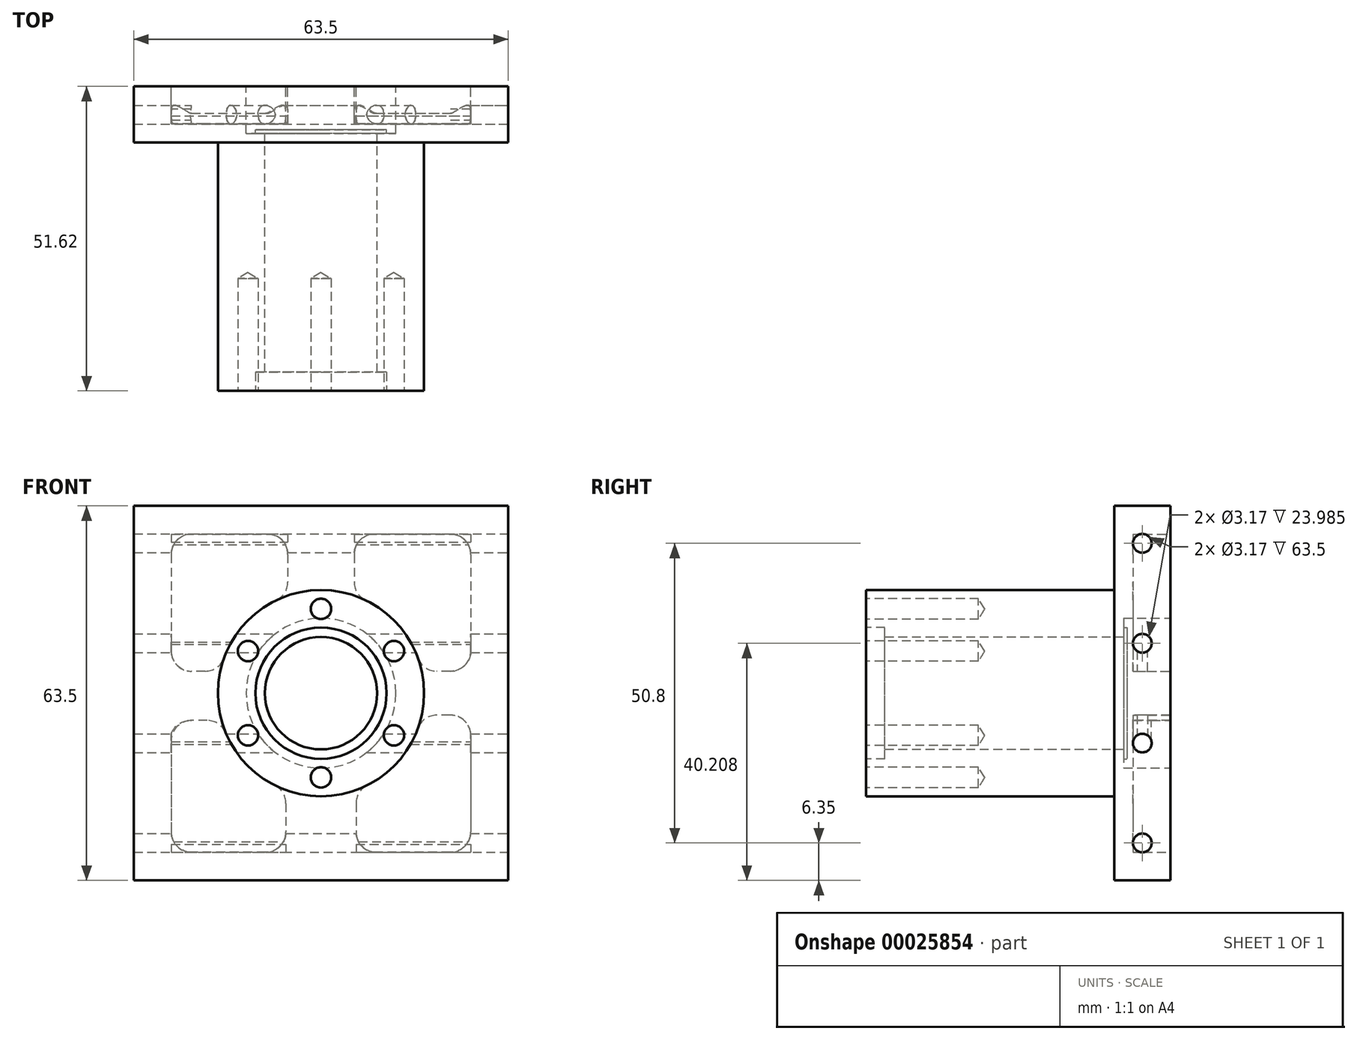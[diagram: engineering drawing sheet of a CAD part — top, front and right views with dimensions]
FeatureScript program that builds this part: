
annotation { "Feature Type Name" : "Feature", "Feature Type Description" : "" }
export const myFeature = defineFeature(function(context is Context, id is Id, definition is map)
    precondition{}
    {
        {
            var Q0;
            Q0=qCreatedBy(makeId("Front.planeOp"),FACE);
            var sketch = newSketch(context, id + "F0", { "sketchPlane" : qUnion([Q0])});
            skLineSegment(sketch, "E0.rect.bottom", {"start": v(-31.75, 31.75) * mm, "end": v(31.75, 31.75) * mm});
            skLineSegment(sketch, "E0.rect.top", {"start": v(-31.75, -31.75) * mm, "end": v(31.75, -31.75) * mm});
            skLineSegment(sketch, "E0.rect.left", {"start": v(-31.75, 31.75) * mm, "end": v(-31.75, -31.75) * mm});
            skLineSegment(sketch, "E0.rect.right", {"start": v(31.75, 31.75) * mm, "end": v(31.75, -31.75) * mm});
            skPoint(sketch, "E0.rect.middle", {"position": v(0, 0) * mm});
            skSolve(sketch);
        }
        {
            var Q0;
            Q0 = qSketchRegion(id + "F0", true);
            extrude(context, id + "F1", {"entities" : qUnion([Q0]), "oppositeDirection" : true, "depth" : 9.52 * mm});
        }
        {
            var Q0;
            Q0=makeQuery(id+"F1.opExtrude","SWEPT_FACE",FACE,{"disambiguationData":[OSD([sQuery(id+"F0.wireOp",EDGE,"E0.rect.right")])]});
            var sketch = newSketch(context, id + "F2", { "sketchPlane" : qUnion([Q0])});
            skLineSegment(sketch, "E1", {"start": v(4.75, 33.77) * mm, "end": v(4.75, -39.78) * mm});
            skPoint(sketch, "E2", {"position": v(4.75, 25.4) * mm});
            skPoint(sketch, "E3", {"position": v(4.75, 8.46) * mm});
            skPoint(sketch, "E4", {"position": v(4.75, -8.46) * mm});
            skPoint(sketch, "E5", {"position": v(4.75, -25.4) * mm});
            skSolve(sketch);
        }
        {
            var Q0;
            Q0=sQuery(id+"F2.wireOp",VERTEX,"E2");
            var Q1;
            Q1=sQuery(id+"F2.wireOp",VERTEX,"E3");
            var Q2;
            Q2=sQuery(id+"F2.wireOp",VERTEX,"E4");
            var Q3;
            Q3=sQuery(id+"F2.wireOp",VERTEX,"E5");
            var Q4;
            Q4=makeQuery(id+"F1.opExtrude","SWEPT_BODY",BODY,{"disambiguationData":[OSD([sQuery(id+"F0.wireOp",EDGE,"E0.rect.bottom"),sQuery(id+"F0.wireOp",EDGE,"E0.rect.top"),sQuery(id+"F0.wireOp",EDGE,"E0.rect.left"),sQuery(id+"F0.wireOp",EDGE,"E0.rect.right")])]});
            hole(context, id + "F3", {"style" : HoleStyle.SIMPLE, "holeDiameter" : 3.17 * mm, "endStyle" : HoleEndStyle.THROUGH, "locations" : qUnion([Q0, Q1, Q2, Q3]), "scope" : qUnion([Q4])});
        }
        {
            var Q0;
            Q0=makeQuery(id+"F1.opExtrude","CAP_FACE",FACE,{"disambiguationData":[OSD([sQuery(id+"F0.wireOp",EDGE,"E0.rect.bottom"),sQuery(id+"F0.wireOp",EDGE,"E0.rect.top"),sQuery(id+"F0.wireOp",EDGE,"E0.rect.left"),sQuery(id+"F0.wireOp",EDGE,"E0.rect.right")])],"isStart":true});
            var sketch = newSketch(context, id + "F4", { "sketchPlane" : qUnion([Q0])});
            skCircle(sketch, "E6", {"center": v(0, 0) * mm, "radius": 17.49 * mm});
            skSolve(sketch);
        }
        {
            var Q0;
            Q0 = qSketchRegion(id + "F4", true);
            extrude(context, id + "F5", {"entities" : qUnion([Q0]), "operationType" : NewBodyOperationType.ADD, "depth" : 42.1 * mm});
        }
        {
            var Q0;
            Q0=makeQuery(id+"F5.opExtrude","CAP_FACE",FACE,{"disambiguationData":[OSD([sQuery(id+"F4.wireOp",EDGE,"E6")])],"isStart":false});
            var sketch = newSketch(context, id + "F6", { "sketchPlane" : qUnion([Q0])});
            skCircle(sketch, "E7", {"center": v(0, 0) * mm, "radius": 14.29 * mm});
            skCircle(sketch, "E8.cCircle", {"center": v(0, 0) * mm, "radius": 14.29 * mm, "construction": true});
            skLineSegment(sketch, "E8.0", {"start": v(0, 14.29) * mm, "end": v(12.37, 7.14) * mm});
            skLineSegment(sketch, "E8.1", {"start": v(12.37, 7.14) * mm, "end": v(12.37, -7.14) * mm});
            skLineSegment(sketch, "E8.2", {"start": v(12.37, -7.14) * mm, "end": v(0, -14.29) * mm});
            skLineSegment(sketch, "E8.3", {"start": v(0, -14.29) * mm, "end": v(-12.37, -7.14) * mm});
            skLineSegment(sketch, "E8.4", {"start": v(-12.37, -7.14) * mm, "end": v(-12.37, 7.14) * mm});
            skLineSegment(sketch, "E8.5", {"start": v(-12.37, 7.14) * mm, "end": v(0, 14.29) * mm});
            skSolve(sketch);
        }
        {
            var Q0;
            Q0=sQuery(id+"F6.wireOp",VERTEX,"E8.0.start");
            var Q1;
            Q1=sQuery(id+"F6.wireOp",VERTEX,"E8.4.end");
            var Q2;
            Q2=sQuery(id+"F6.wireOp",VERTEX,"E8.3.end");
            var Q3;
            Q3=sQuery(id+"F6.wireOp",VERTEX,"E8.3.start");
            var Q4;
            Q4=sQuery(id+"F6.wireOp",VERTEX,"E8.2.start");
            var Q5;
            Q5=sQuery(id+"F6.wireOp",VERTEX,"E8.1.start");
            var Q6;
            Q6=makeQuery(id+"F1.opExtrude","SWEPT_BODY",BODY,{"disambiguationData":[OSD([sQuery(id+"F0.wireOp",EDGE,"E0.rect.bottom"),sQuery(id+"F0.wireOp",EDGE,"E0.rect.top"),sQuery(id+"F0.wireOp",EDGE,"E0.rect.left"),sQuery(id+"F0.wireOp",EDGE,"E0.rect.right")])]});
            hole(context, id + "F7", {"style" : HoleStyle.SIMPLE, "holeDiameter" : 3.45 * mm, "endStyle" : HoleEndStyle.BLIND, "holeDepth" : 19.05 * mm, "locations" : qUnion([Q0, Q1, Q2, Q3, Q4, Q5]), "scope" : qUnion([Q6])});
        }
        {
            var Q0;
            Q0=makeQuery(id+"F1.opExtrude","CAP_FACE",FACE,{"disambiguationData":[OSD([sQuery(id+"F0.wireOp",EDGE,"E0.rect.bottom"),sQuery(id+"F0.wireOp",EDGE,"E0.rect.top"),sQuery(id+"F0.wireOp",EDGE,"E0.rect.left"),sQuery(id+"F0.wireOp",EDGE,"E0.rect.right")])],"isStart":false});
            var sketch = newSketch(context, id + "F8", { "sketchPlane" : qUnion([Q0])});
            skCircle(sketch, "E9", {"center": v(0, 0) * mm, "radius": 9.53 * mm});
            skSolve(sketch);
        }
        {
            var Q0;
            Q0 = qSketchRegion(id + "F8", true);
            extrude(context, id + "F9", {"entities" : qUnion([Q0]), "operationType" : NewBodyOperationType.REMOVE, "oppositeDirection" : true, "depth" : 71.13 * mm});
        }
        {
            var Q0;
            Q0=makeQuery(id+"F1.opExtrude","CAP_FACE",FACE,{"disambiguationData":[OSD([sQuery(id+"F0.wireOp",EDGE,"E0.rect.bottom"),sQuery(id+"F0.wireOp",EDGE,"E0.rect.top"),sQuery(id+"F0.wireOp",EDGE,"E0.rect.left"),sQuery(id+"F0.wireOp",EDGE,"E0.rect.right")])],"isStart":false});
            var sketch = newSketch(context, id + "F10", { "sketchPlane" : qUnion([Q0])});
            skCircle(sketch, "E10", {"center": v(0, 0) * mm, "radius": 11.13 * mm});
            skSolve(sketch);
        }
        {
            var Q0;
            Q0 = qSketchRegion(id + "F10", true);
            extrude(context, id + "F11", {"entities" : qUnion([Q0]), "operationType" : NewBodyOperationType.REMOVE, "oppositeDirection" : true, "depth" : 7.37 * mm});
        }
        {
            var Q0;
            Q0=makeQuery(id+"F1.opExtrude","CAP_FACE",FACE,{"disambiguationData":[OSD([sQuery(id+"F0.wireOp",EDGE,"E0.rect.bottom"),sQuery(id+"F0.wireOp",EDGE,"E0.rect.top"),sQuery(id+"F0.wireOp",EDGE,"E0.rect.left"),sQuery(id+"F0.wireOp",EDGE,"E0.rect.right")])],"isStart":false});
            var sketch = newSketch(context, id + "F12", { "sketchPlane" : qUnion([Q0])});
            skCircle(sketch, "E11", {"center": v(0, 0) * mm, "radius": 12.7 * mm});
            skSolve(sketch);
        }
        {
            var Q0;
            Q0=makeQuery(id+"F12.imprint","IMPRINT",FACE,{"disambiguationData":[TD([[makeQuery(id+"F12.imprint","IMPRINT",EDGE,{"derivedFrom":sQuery(id+"F12.wireOp",EDGE,"E11")}),1.0]])]});
            extrude(context, id + "F13", {"entities" : qUnion([Q0]), "operationType" : NewBodyOperationType.REMOVE, "oppositeDirection" : true, "depth" : 7.95 * mm});
        }
        {
            var Q0;
            Q0=makeQuery(id+"F5.opExtrude","CAP_FACE",FACE,{"disambiguationData":[OSD([sQuery(id+"F4.wireOp",EDGE,"E6")])],"isStart":false});
            var sketch = newSketch(context, id + "F14", { "sketchPlane" : qUnion([Q0])});
            skCircle(sketch, "E12", {"center": v(0, 0) * mm, "radius": 11.13 * mm});
            skSolve(sketch);
        }
        {
            var Q0;
            Q0 = qSketchRegion(id + "F14", true);
            extrude(context, id + "F15", {"entities" : qUnion([Q0]), "operationType" : NewBodyOperationType.REMOVE, "oppositeDirection" : true, "depth" : 3.17 * mm});
        }
        {
            var Q0;
            Q0=makeQuery(id+"F1.opExtrude","CAP_FACE",FACE,{"disambiguationData":[OSD([sQuery(id+"F0.wireOp",EDGE,"E0.rect.bottom"),sQuery(id+"F0.wireOp",EDGE,"E0.rect.top"),sQuery(id+"F0.wireOp",EDGE,"E0.rect.left"),sQuery(id+"F0.wireOp",EDGE,"E0.rect.right")])],"isStart":false});
            var sketch = newSketch(context, id + "F16", { "sketchPlane" : qUnion([Q0])});
            skLineSegment(sketch, "E13.rect.bottom", {"start": v(-25.4, 26.97) * mm, "end": v(-5.63, 26.97) * mm});
            skLineSegment(sketch, "E13.rect.top", {"start": v(-25.4, -26.97) * mm, "end": v(-5.95, -26.97) * mm});
            skLineSegment(sketch, "E13.rect.left", {"start": v(-25.4, 26.97) * mm, "end": v(-25.4, 3.73) * mm});
            skLineSegment(sketch, "E13.rect.right", {"start": v(25.4, 26.97) * mm, "end": v(25.4, 3.73) * mm});
            skPoint(sketch, "E13.rect.middle", {"position": v(0, 0) * mm});
            skArc(sketch, "E14", {"start": v(-5.63, 16.54) * mm, "mid": v(-13.04, 11.64) * mm, "end": v(-17.07, 3.73) * mm});
            skLineSegment(sketch, "E15", {"start": v(-5.63, 26.97) * mm, "end": v(-5.63, 16.54) * mm});
            skLineSegment(sketch, "E16", {"start": v(5.63, 26.97) * mm, "end": v(5.63, 16.54) * mm});
            skLineSegment(sketch, "E17", {"start": v(5.95, -16.43) * mm, "end": v(5.95, -26.97) * mm});
            skLineSegment(sketch, "E18", {"start": v(-5.95, -16.43) * mm, "end": v(-5.95, -26.97) * mm});
            skLineSegment(sketch, "E19", {"start": v(-25.4, -3.73) * mm, "end": v(-17.07, -3.73) * mm});
            skLineSegment(sketch, "E20", {"start": v(-25.4, 3.73) * mm, "end": v(-17.07, 3.73) * mm});
            skLineSegment(sketch, "E21", {"start": v(17.07, 3.73) * mm, "end": v(25.4, 3.73) * mm});
            skLineSegment(sketch, "E22", {"start": v(16.85, -4.63) * mm, "end": v(25.4, -4.63) * mm});
            skLineSegment(sketch, "E23.trimOffspring", {"start": v(5.63, 26.97) * mm, "end": v(25.4, 26.97) * mm});
            skArc(sketch, "E24.trimOffspring", {"start": v(-17.07, -3.73) * mm, "mid": v(-13.15, -11.51) * mm, "end": v(-5.95, -16.43) * mm});
            skLineSegment(sketch, "E25.trimOffspring", {"start": v(-25.4, -3.73) * mm, "end": v(-25.4, -26.97) * mm});
            skArc(sketch, "E26.trimOffspring", {"start": v(5.95, -16.43) * mm, "mid": v(12.84, -11.86) * mm, "end": v(16.85, -4.63) * mm});
            skLineSegment(sketch, "E27.trimOffspring", {"start": v(5.95, -26.97) * mm, "end": v(25.4, -26.97) * mm});
            skLineSegment(sketch, "E28.trimOffspring", {"start": v(25.4, -4.63) * mm, "end": v(25.4, -26.97) * mm});
            skArc(sketch, "E29.trimOffspring", {"start": v(17.07, 3.73) * mm, "mid": v(13.04, 11.64) * mm, "end": v(5.63, 16.54) * mm});
            skSolve(sketch);
        }
        {
            var Q0;
            Q0=makeQuery(id+"F16.imprint","IMPRINT",FACE,{"disambiguationData":[TD([[makeQuery(id+"F16.imprint","IMPRINT",EDGE,{"derivedFrom":sQuery(id+"F16.wireOp",EDGE,"E13.rect.bottom")}),-1.0]])]});
            var Q1;
            Q1=makeQuery(id+"F16.imprint","IMPRINT",FACE,{"disambiguationData":[TD([[makeQuery(id+"F16.imprint","IMPRINT",EDGE,{"derivedFrom":sQuery(id+"F16.wireOp",EDGE,"E13.rect.right")}),-1.0]])]});
            var Q2;
            Q2=makeQuery(id+"F16.imprint","IMPRINT",FACE,{"disambiguationData":[TD([[makeQuery(id+"F16.imprint","IMPRINT",EDGE,{"derivedFrom":sQuery(id+"F16.wireOp",EDGE,"E17")}),1.0]])]});
            var Q3;
            Q3=makeQuery(id+"F16.imprint","IMPRINT",FACE,{"disambiguationData":[TD([[makeQuery(id+"F16.imprint","IMPRINT",EDGE,{"derivedFrom":sQuery(id+"F16.wireOp",EDGE,"E13.rect.top")}),1.0]])]});
            extrude(context, id + "F17", {"entities" : qUnion([Q0, Q1, Q2, Q3]), "operationType" : NewBodyOperationType.REMOVE, "oppositeDirection" : true, "depth" : 6.35 * mm});
        }
        {
            var Q0;
            {var subQ0=sQuery(id+"F16.wireOp",EDGE,"E13.rect.bottom");var subQ1=sQuery(id+"F16.wireOp",EDGE,"E13.rect.left");Q0=makeQuery(id+"F17.boolean.opBoolean","COPY",EDGE,{"disambiguationData":[TD([makeQuery(id+"F1.opExtrude","CAP_FACE",FACE,{"disambiguationData":[OSD([sQuery(id+"F0.wireOp",EDGE,"E0.rect.bottom"),sQuery(id+"F0.wireOp",EDGE,"E0.rect.top"),sQuery(id+"F0.wireOp",EDGE,"E0.rect.left"),sQuery(id+"F0.wireOp",EDGE,"E0.rect.right")])],"isStart":false})])],"derivedFrom":makeQuery(id+"F17.opExtrude","SWEPT_EDGE",EDGE,{"disambiguationData":[OSD([subQ0,subQ1])]})});}
            var Q1;
            {var subQ0=sQuery(id+"F16.wireOp",EDGE,"E16");var subQ1=sQuery(id+"F16.wireOp",EDGE,"E23.trimOffspring");Q1=makeQuery(id+"F17.boolean.opBoolean","COPY",EDGE,{"disambiguationData":[TD([makeQuery(id+"F1.opExtrude","CAP_FACE",FACE,{"disambiguationData":[OSD([sQuery(id+"F0.wireOp",EDGE,"E0.rect.bottom"),sQuery(id+"F0.wireOp",EDGE,"E0.rect.top"),sQuery(id+"F0.wireOp",EDGE,"E0.rect.left"),sQuery(id+"F0.wireOp",EDGE,"E0.rect.right")])],"isStart":false})])],"derivedFrom":makeQuery(id+"F17.opExtrude","SWEPT_EDGE",EDGE,{"disambiguationData":[OSD([subQ0,subQ1])]})});}
            var Q2;
            Q2=makeQuery(id+"F17.boolean.opBoolean","COPY",EDGE,{"derivedFrom":makeQuery(id+"F17.opExtrude","SWEPT_EDGE",EDGE,{"disambiguationData":[OSD([sQuery(id+"F16.wireOp",EDGE,"E17"),sQuery(id+"F16.wireOp",EDGE,"E26.trimOffspring")])]})});
            var Q3;
            Q3=makeQuery(id+"F17.boolean.opBoolean","COPY",EDGE,{"derivedFrom":makeQuery(id+"F17.opExtrude","SWEPT_EDGE",EDGE,{"disambiguationData":[OSD([sQuery(id+"F16.wireOp",EDGE,"E22"),sQuery(id+"F16.wireOp",EDGE,"E26.trimOffspring")])]})});
            var Q4;
            Q4=makeQuery(id+"F17.boolean.opBoolean","COPY",EDGE,{"derivedFrom":makeQuery(id+"F17.opExtrude","SWEPT_EDGE",EDGE,{"disambiguationData":[OSD([sQuery(id+"F16.wireOp",EDGE,"E19"),sQuery(id+"F16.wireOp",EDGE,"E25.trimOffspring")])]})});
            var Q5;
            Q5=makeQuery(id+"F17.boolean.opBoolean","COPY",EDGE,{"derivedFrom":makeQuery(id+"F17.opExtrude","SWEPT_EDGE",EDGE,{"disambiguationData":[OSD([sQuery(id+"F16.wireOp",EDGE,"E13.rect.left"),sQuery(id+"F16.wireOp",EDGE,"E20")])]})});
            var Q6;
            Q6=makeQuery(id+"F17.boolean.opBoolean","COPY",EDGE,{"derivedFrom":makeQuery(id+"F17.opExtrude","SWEPT_EDGE",EDGE,{"disambiguationData":[OSD([sQuery(id+"F16.wireOp",EDGE,"E14"),sQuery(id+"F16.wireOp",EDGE,"E20")])]})});
            var Q7;
            Q7=makeQuery(id+"F17.boolean.opBoolean","COPY",EDGE,{"derivedFrom":makeQuery(id+"F17.opExtrude","SWEPT_EDGE",EDGE,{"disambiguationData":[OSD([sQuery(id+"F16.wireOp",EDGE,"E14"),sQuery(id+"F16.wireOp",EDGE,"E15")])]})});
            var Q8;
            {var subQ0=sQuery(id+"F16.wireOp",EDGE,"E13.rect.bottom");var subQ1=sQuery(id+"F16.wireOp",EDGE,"E15");Q8=makeQuery(id+"F17.boolean.opBoolean","COPY",EDGE,{"disambiguationData":[TD([makeQuery(id+"F1.opExtrude","CAP_FACE",FACE,{"disambiguationData":[OSD([sQuery(id+"F0.wireOp",EDGE,"E0.rect.bottom"),sQuery(id+"F0.wireOp",EDGE,"E0.rect.top"),sQuery(id+"F0.wireOp",EDGE,"E0.rect.left"),sQuery(id+"F0.wireOp",EDGE,"E0.rect.right")])],"isStart":false})])],"derivedFrom":makeQuery(id+"F17.opExtrude","SWEPT_EDGE",EDGE,{"disambiguationData":[OSD([subQ0,subQ1])]})});}
            var Q9;
            {var subQ0=sQuery(id+"F16.wireOp",EDGE,"E13.rect.right");var subQ1=sQuery(id+"F16.wireOp",EDGE,"E23.trimOffspring");Q9=makeQuery(id+"F17.boolean.opBoolean","COPY",EDGE,{"disambiguationData":[TD([makeQuery(id+"F1.opExtrude","CAP_FACE",FACE,{"disambiguationData":[OSD([sQuery(id+"F0.wireOp",EDGE,"E0.rect.bottom"),sQuery(id+"F0.wireOp",EDGE,"E0.rect.top"),sQuery(id+"F0.wireOp",EDGE,"E0.rect.left"),sQuery(id+"F0.wireOp",EDGE,"E0.rect.right")])],"isStart":false})])],"derivedFrom":makeQuery(id+"F17.opExtrude","SWEPT_EDGE",EDGE,{"disambiguationData":[OSD([subQ0,subQ1])]})});}
            var Q10;
            Q10=makeQuery(id+"F17.boolean.opBoolean","COPY",EDGE,{"derivedFrom":makeQuery(id+"F17.opExtrude","SWEPT_EDGE",EDGE,{"disambiguationData":[OSD([sQuery(id+"F16.wireOp",EDGE,"E13.rect.right"),sQuery(id+"F16.wireOp",EDGE,"E21")])]})});
            var Q11;
            Q11=makeQuery(id+"F17.boolean.opBoolean","COPY",EDGE,{"derivedFrom":makeQuery(id+"F17.opExtrude","SWEPT_EDGE",EDGE,{"disambiguationData":[OSD([sQuery(id+"F16.wireOp",EDGE,"E21"),sQuery(id+"F16.wireOp",EDGE,"E29.trimOffspring")])]})});
            var Q12;
            Q12=makeQuery(id+"F17.boolean.opBoolean","COPY",EDGE,{"derivedFrom":makeQuery(id+"F17.opExtrude","SWEPT_EDGE",EDGE,{"disambiguationData":[OSD([sQuery(id+"F16.wireOp",EDGE,"E16"),sQuery(id+"F16.wireOp",EDGE,"E29.trimOffspring")])]})});
            var Q13;
            {var subQ0=sQuery(id+"F16.wireOp",EDGE,"E27.trimOffspring");var subQ1=sQuery(id+"F16.wireOp",EDGE,"E17");Q13=makeQuery(id+"F17.boolean.opBoolean","COPY",EDGE,{"disambiguationData":[TD([makeQuery(id+"F1.opExtrude","CAP_FACE",FACE,{"disambiguationData":[OSD([sQuery(id+"F0.wireOp",EDGE,"E0.rect.bottom"),sQuery(id+"F0.wireOp",EDGE,"E0.rect.top"),sQuery(id+"F0.wireOp",EDGE,"E0.rect.left"),sQuery(id+"F0.wireOp",EDGE,"E0.rect.right")])],"isStart":false})])],"derivedFrom":makeQuery(id+"F17.opExtrude","SWEPT_EDGE",EDGE,{"disambiguationData":[OSD([subQ1,subQ0])]})});}
            var Q14;
            {var subQ0=sQuery(id+"F16.wireOp",EDGE,"E27.trimOffspring");var subQ1=sQuery(id+"F16.wireOp",EDGE,"E28.trimOffspring");Q14=makeQuery(id+"F17.boolean.opBoolean","COPY",EDGE,{"disambiguationData":[TD([makeQuery(id+"F1.opExtrude","CAP_FACE",FACE,{"disambiguationData":[OSD([sQuery(id+"F0.wireOp",EDGE,"E0.rect.bottom"),sQuery(id+"F0.wireOp",EDGE,"E0.rect.top"),sQuery(id+"F0.wireOp",EDGE,"E0.rect.left"),sQuery(id+"F0.wireOp",EDGE,"E0.rect.right")])],"isStart":false})])],"derivedFrom":makeQuery(id+"F17.opExtrude","SWEPT_EDGE",EDGE,{"disambiguationData":[OSD([subQ0,subQ1])]})});}
            var Q15;
            Q15=makeQuery(id+"F17.boolean.opBoolean","COPY",EDGE,{"derivedFrom":makeQuery(id+"F17.opExtrude","SWEPT_EDGE",EDGE,{"disambiguationData":[OSD([sQuery(id+"F16.wireOp",EDGE,"E22"),sQuery(id+"F16.wireOp",EDGE,"E28.trimOffspring")])]})});
            var Q16;
            {var subQ0=sQuery(id+"F16.wireOp",EDGE,"E13.rect.top");var subQ1=sQuery(id+"F16.wireOp",EDGE,"E25.trimOffspring");Q16=makeQuery(id+"F17.boolean.opBoolean","COPY",EDGE,{"disambiguationData":[TD([makeQuery(id+"F1.opExtrude","CAP_FACE",FACE,{"disambiguationData":[OSD([sQuery(id+"F0.wireOp",EDGE,"E0.rect.bottom"),sQuery(id+"F0.wireOp",EDGE,"E0.rect.top"),sQuery(id+"F0.wireOp",EDGE,"E0.rect.left"),sQuery(id+"F0.wireOp",EDGE,"E0.rect.right")])],"isStart":false})])],"derivedFrom":makeQuery(id+"F17.opExtrude","SWEPT_EDGE",EDGE,{"disambiguationData":[OSD([subQ0,subQ1])]})});}
            var Q17;
            Q17=makeQuery(id+"F17.boolean.opBoolean","COPY",EDGE,{"derivedFrom":makeQuery(id+"F17.opExtrude","SWEPT_EDGE",EDGE,{"disambiguationData":[OSD([sQuery(id+"F16.wireOp",EDGE,"E18"),sQuery(id+"F16.wireOp",EDGE,"E24.trimOffspring")])]})});
            var Q18;
            Q18=makeQuery(id+"F17.boolean.opBoolean","COPY",EDGE,{"derivedFrom":makeQuery(id+"F17.opExtrude","SWEPT_EDGE",EDGE,{"disambiguationData":[OSD([sQuery(id+"F16.wireOp",EDGE,"E19"),sQuery(id+"F16.wireOp",EDGE,"E24.trimOffspring")])]})});
            var Q19;
            {var subQ0=sQuery(id+"F16.wireOp",EDGE,"E13.rect.top");var subQ1=sQuery(id+"F16.wireOp",EDGE,"E18");Q19=makeQuery(id+"F17.boolean.opBoolean","COPY",EDGE,{"disambiguationData":[TD([makeQuery(id+"F1.opExtrude","CAP_FACE",FACE,{"disambiguationData":[OSD([sQuery(id+"F0.wireOp",EDGE,"E0.rect.bottom"),sQuery(id+"F0.wireOp",EDGE,"E0.rect.top"),sQuery(id+"F0.wireOp",EDGE,"E0.rect.left"),sQuery(id+"F0.wireOp",EDGE,"E0.rect.right")])],"isStart":false})])],"derivedFrom":makeQuery(id+"F17.opExtrude","SWEPT_EDGE",EDGE,{"disambiguationData":[OSD([subQ0,subQ1])]})});}
            fillet(context, id + "F18", {"entities" : qUnion([Q0, Q1, Q2, Q3, Q4, Q5, Q6, Q7, Q8, Q9, Q10, Q11, Q12, Q13, Q14, Q15, Q16, Q17, Q18, Q19]), "radius" : 3.43 * mm, "tangentPropagation" : true, "allowEdgeOverflow" : false});
        }
    });
